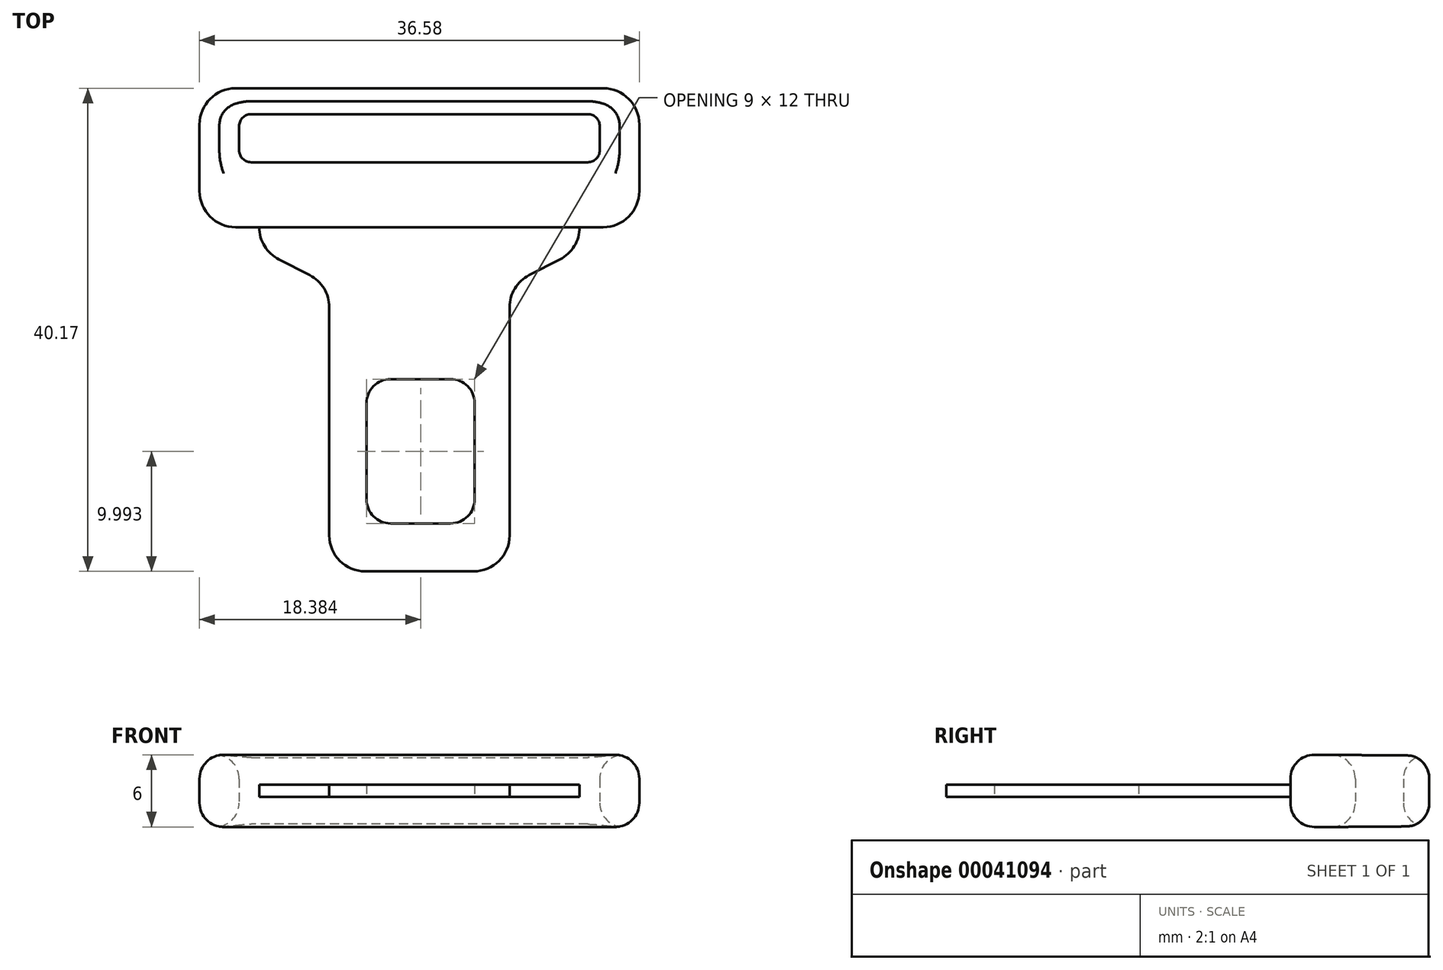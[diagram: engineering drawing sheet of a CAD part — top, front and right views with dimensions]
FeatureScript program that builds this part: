
annotation { "Feature Type Name" : "Feature", "Feature Type Description" : "" }
export const myFeature = defineFeature(function(context is Context, id is Id, definition is map)
    precondition{}
    {
        {
            var Q0;
            Q0=qCreatedBy(makeId("Top.planeOp"),FACE);
            var sketch = newSketch(context, id + "F0", { "sketchPlane" : qUnion([Q0])});
            skLineSegment(sketch, "E0.top", {"start": v(-4.5, -23.8) * mm, "end": v(4.5, -23.8) * mm});
            skLineSegment(sketch, "E0.left", {"start": v(-7.5, -3.8) * mm, "end": v(-7.5, -20.8) * mm});
            skLineSegment(sketch, "E0.right", {"start": v(7.5, -3.8) * mm, "end": v(7.5, -20.8) * mm});
            skPoint(sketch, "E1", {"position": v(0.1, -3.8) * mm});
            skPoint(sketch, "E2.visualSharp", {"position": v(-7.5, -23.8) * mm});
            skArc(sketch, "E2.filletArc", {"start": v(-7.5, -20.8) * mm, "mid": v(-6.62, -22.92) * mm, "end": v(-4.5, -23.8) * mm});
            skPoint(sketch, "E3.visualSharp", {"position": v(7.5, -23.8) * mm});
            skArc(sketch, "E3.filletArc", {"start": v(4.5, -23.8) * mm, "mid": v(6.62, -22.92) * mm, "end": v(7.5, -20.8) * mm});
            skLineSegment(sketch, "E4", {"start": v(7.5, -3.8) * mm, "end": v(7.5, -1.83) * mm});
            skLineSegment(sketch, "E5", {"start": v(9.13, 0.84) * mm, "end": v(11.7, 2.15) * mm});
            skPoint(sketch, "E6.visualSharp", {"position": v(7.5, 0) * mm});
            skArc(sketch, "E6.filletArc", {"start": v(9.13, 0.84) * mm, "mid": v(7.94, -0.27) * mm, "end": v(7.5, -1.83) * mm});
            skPoint(sketch, "E7.visualSharp", {"position": v(13.32, 2.99) * mm});
            skArc(sketch, "E7.filletArc", {"start": v(11.7, 2.15) * mm, "mid": v(12.88, 3.26) * mm, "end": v(13.32, 4.82) * mm});
            skLineSegment(sketch, "E8.bottom", {"start": v(0, 4.82) * mm, "end": v(15.3, 4.82) * mm});
            skLineSegment(sketch, "E8.top", {"start": v(0, 16.37) * mm, "end": v(15.3, 16.37) * mm});
            skLineSegment(sketch, "E8.left", {"start": v(0, 4.82) * mm, "end": v(0, 16.37) * mm});
            skLineSegment(sketch, "E8.right", {"start": v(18.3, 7.82) * mm, "end": v(18.3, 13.37) * mm});
            skLineSegment(sketch, "E9.MirrorCS", {"start": v(0, 16.37) * mm, "end": v(-15.3, 16.37) * mm});
            skLineSegment(sketch, "E10.MirrorCS", {"start": v(0, 4.82) * mm, "end": v(-15.3, 4.82) * mm});
            skLineSegment(sketch, "E11.MirrorCS", {"start": v(-18.3, 7.82) * mm, "end": v(-18.3, 13.37) * mm});
            skPoint(sketch, "E12.MirrorP", {"position": v(-13.32, 2.99) * mm});
            skArc(sketch, "E13.MirrorCS", {"start": v(-11.7, 2.15) * mm, "mid": v(-12.88, 3.26) * mm, "end": v(-13.32, 4.82) * mm});
            skLineSegment(sketch, "E14.MirrorCS", {"start": v(-9.13, 0.84) * mm, "end": v(-11.7, 2.15) * mm});
            skArc(sketch, "E15.MirrorCS", {"start": v(-9.13, 0.84) * mm, "mid": v(-7.94, -0.27) * mm, "end": v(-7.5, -1.83) * mm});
            skLineSegment(sketch, "E16.MirrorCS", {"start": v(-7.5, -3.8) * mm, "end": v(-7.5, -1.83) * mm});
            skLineSegment(sketch, "E17.bottom", {"start": v(-2.4, -7.8) * mm, "end": v(2.6, -7.8) * mm});
            skLineSegment(sketch, "E17.top", {"start": v(-2.4, -19.8) * mm, "end": v(2.6, -19.8) * mm});
            skLineSegment(sketch, "E17.left", {"start": v(-4.4, -9.8) * mm, "end": v(-4.4, -17.8) * mm});
            skLineSegment(sketch, "E17.right", {"start": v(4.6, -9.8) * mm, "end": v(4.6, -17.8) * mm});
            skPoint(sketch, "E18.visualSharp", {"position": v(-4.4, -7.8) * mm});
            skArc(sketch, "E18.filletArc", {"start": v(-2.4, -7.8) * mm, "mid": v(-3.82, -8.4) * mm, "end": v(-4.4, -9.8) * mm});
            skPoint(sketch, "E19.visualSharp", {"position": v(4.6, -7.8) * mm});
            skArc(sketch, "E19.filletArc", {"start": v(4.6, -9.8) * mm, "mid": v(4, -8.4) * mm, "end": v(2.6, -7.8) * mm});
            skPoint(sketch, "E20.visualSharp", {"position": v(4.6, -19.8) * mm});
            skArc(sketch, "E20.filletArc", {"start": v(2.6, -19.8) * mm, "mid": v(4, -19.22) * mm, "end": v(4.6, -17.8) * mm});
            skPoint(sketch, "E21.visualSharp", {"position": v(-4.4, -19.8) * mm});
            skArc(sketch, "E21.filletArc", {"start": v(-4.4, -17.8) * mm, "mid": v(-3.82, -19.22) * mm, "end": v(-2.4, -19.8) * mm});
            skPoint(sketch, "E22", {"position": v(0.1, -7.8) * mm});
            skPoint(sketch, "E23.MirrorCS.end.orphan", {"position": v(-13.32, 6.3) * mm});
            skPoint(sketch, "E23.MirrorCS.start.orphan", {"position": v(-13.32, 4.82) * mm});
            skPoint(sketch, "E24.end.orphan", {"position": v(0, 6.3) * mm});
            skPoint(sketch, "E25.end.orphan", {"position": v(13.32, 6.3) * mm});
            skPoint(sketch, "E26.visualSharp", {"position": v(-18.3, 16.37) * mm});
            skArc(sketch, "E26.filletArc", {"start": v(-15.3, 16.37) * mm, "mid": v(-17.41, 15.5) * mm, "end": v(-18.3, 13.37) * mm});
            skPoint(sketch, "E27.visualSharp", {"position": v(-18.3, 4.82) * mm});
            skArc(sketch, "E27.filletArc", {"start": v(-18.3, 7.82) * mm, "mid": v(-17.41, 5.7) * mm, "end": v(-15.3, 4.82) * mm});
            skPoint(sketch, "E28.visualSharp", {"position": v(18.3, 4.82) * mm});
            skArc(sketch, "E28.filletArc", {"start": v(15.3, 4.82) * mm, "mid": v(17.41, 5.7) * mm, "end": v(18.3, 7.82) * mm});
            skPoint(sketch, "E29.visualSharp", {"position": v(18.3, 16.37) * mm});
            skArc(sketch, "E29.filletArc", {"start": v(18.3, 13.37) * mm, "mid": v(17.41, 15.5) * mm, "end": v(15.3, 16.37) * mm});
            skLineSegment(sketch, "E30.bottom", {"start": v(-14, 14.23) * mm, "end": v(14, 14.23) * mm});
            skLineSegment(sketch, "E30.top", {"start": v(-14, 10.23) * mm, "end": v(14, 10.23) * mm});
            skLineSegment(sketch, "E30.left", {"start": v(-15, 13.23) * mm, "end": v(-15, 11.23) * mm});
            skLineSegment(sketch, "E30.right", {"start": v(15, 13.23) * mm, "end": v(15, 11.23) * mm});
            skPoint(sketch, "E31", {"position": v(0, 14.23) * mm});
            skPoint(sketch, "E32.visualSharp", {"position": v(-15, 14.23) * mm});
            skArc(sketch, "E32.filletArc", {"start": v(-14, 14.23) * mm, "mid": v(-14.7, 13.93) * mm, "end": v(-15, 13.23) * mm});
            skPoint(sketch, "E33.visualSharp", {"position": v(-15, 10.23) * mm});
            skArc(sketch, "E33.filletArc", {"start": v(-15, 11.23) * mm, "mid": v(-14.7, 10.52) * mm, "end": v(-14, 10.23) * mm});
            skPoint(sketch, "E34.visualSharp", {"position": v(15, 10.23) * mm});
            skArc(sketch, "E34.filletArc", {"start": v(14, 10.23) * mm, "mid": v(14.7, 10.52) * mm, "end": v(15, 11.23) * mm});
            skPoint(sketch, "E35.visualSharp", {"position": v(15, 14.23) * mm});
            skArc(sketch, "E35.filletArc", {"start": v(15, 13.23) * mm, "mid": v(14.7, 13.93) * mm, "end": v(14, 14.23) * mm});
            skSolve(sketch);
        }
        {
            var Q0;
            Q0=makeQuery(id+"F0.imprint","IMPRINT",FACE,{"disambiguationData":[TD([[makeQuery(id+"F0.imprint","IMPRINT",EDGE,{"derivedFrom":sQuery(id+"F0.wireOp",EDGE,"E0.top")}),1.0]])]});
            extrude(context, id + "F1", {"entities" : qUnion([Q0]), "endBound" : BoundingType.SYMMETRIC, "depth" : 1 * mm});
        }
        {
            var Q0;
            {var subQ7=sQuery(id+"F0.wireOp",EDGE,"E9.MirrorCS");Q0=makeQuery(id+"F0.imprint","IMPRINT",FACE,{"disambiguationData":[TD([[makeQuery(id+"F0.imprint","IMPRINT",EDGE,{"derivedFrom":subQ7}),1.0]])]});}
            var Q1;
            {var subQ7=sQuery(id+"F0.wireOp",EDGE,"E8.top");Q1=makeQuery(id+"F0.imprint","IMPRINT",FACE,{"disambiguationData":[TD([[makeQuery(id+"F0.imprint","IMPRINT",EDGE,{"derivedFrom":subQ7}),-1.0]])]});}
            extrude(context, id + "F2", {"entities" : qUnion([Q0, Q1]), "endBound" : BoundingType.SYMMETRIC, "depth" : 6 * mm});
        }
        {
            var Q0;
            Q0=makeQuery(id+"F2.opExtrude","CAP_EDGE",EDGE,{"disambiguationData":[OSD([sQuery(id+"F0.wireOp",EDGE,"E8.bottom"),sQuery(id+"F0.wireOp",EDGE,"E10.MirrorCS")])],"isStart":false});
            var Q1;
            Q1=makeQuery(id+"F2.opExtrude","CAP_EDGE",EDGE,{"disambiguationData":[OSD([sQuery(id+"F0.wireOp",EDGE,"E8.bottom"),sQuery(id+"F0.wireOp",EDGE,"E10.MirrorCS")])],"isStart":true});
            var Q2;
            Q2=makeQuery(id+"F2.opExtrude","CAP_EDGE",EDGE,{"disambiguationData":[OSD([sQuery(id+"F0.wireOp",EDGE,"E30.bottom")])],"isStart":false});
            var Q3;
            Q3=makeQuery(id+"F2.opExtrude","CAP_EDGE",EDGE,{"disambiguationData":[OSD([sQuery(id+"F0.wireOp",EDGE,"E30.bottom")])],"isStart":true});
            fillet(context, id + "F3", {"entities" : qUnion([Q0, Q1, Q2, Q3]), "radius" : 2 * mm, "tangentPropagation" : true, "allowEdgeOverflow" : false});
        }
    });
